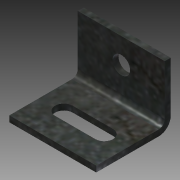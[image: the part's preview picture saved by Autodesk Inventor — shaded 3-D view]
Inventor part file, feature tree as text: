
AUTODESK INVENTOR PART (.ipt)
format: ipt  version: 2015 (Build 190159000, 159)  size: 190,464 bytes
history: native  units: in
note: dims shown in document units (in); Inventor stores cm internally (conversion verified against a paired STEP export)
features: sketch x8, sheet_metal_op x4, projected_geometry x4, other x3, hole x1
ambient origin geometry x8: Origin, YZ Plane, XZ Plane, XY Plane, X Axis, Y Axis, Z Axis, Center Point
bodies: Solid1 (feature_tree)
feature tree (20):
  sheet_metal_op  "Face1"
  sheet_metal_op  "Flange1"
  sketch  "Sketch3"  dims[d3=0.06in]
  hole  "Hole1"  [1 undecoded]
  sketch  "Sketch7"  dims[d5=0.12in]
  sketch  "Sketch8"  dims[d6=0.06in]
  sketch  "Sketch9"  dims[d7=0.625in d8=90.0deg d9=0.06in]
  sketch  "Sketch10"  dims[d10=0.24in d11=0.06in d12=0.06in d13=0.63in d14=0.875in d15=0.875in d16=0.505in d17=0.177in d18=0.75in d19=0.332in d20=0.25in d21=0.5635in d22=0.06in d23=0.8108in d24=0.177in d25=0.146in d26=0.06in d27=0.0in d28=0.625in d29=0.505in d30=0.875in d31=0.75in d32=0.63in d34=0.203in d35=0.281in d36=0.281in]
  sketch  "Sketch1"  dims[d0=0.875in d1=0.75in]
  other  "Plate1"
  sketch  "Sketch2"  dims[d2=0.06in]
  other  "Plate2"
  sheet_metal_op  "Bend1"
  sheet_metal_op  "Corner1"
  projected_geometry  "Projected Loop1"
  sketch  "Sketch4"  dims[d4=0.03in]
  projected_geometry  "Projected Loop2"
  projected_geometry  "Projected Loop3"
  projected_geometry  "Projected Loop4"
  other  "Cut1"
note: 1 required parameter value undecoded (feature->parameter linkage not recoverable at this tier; creation-order binding heuristic only, values carry confidence <= 0.55)
